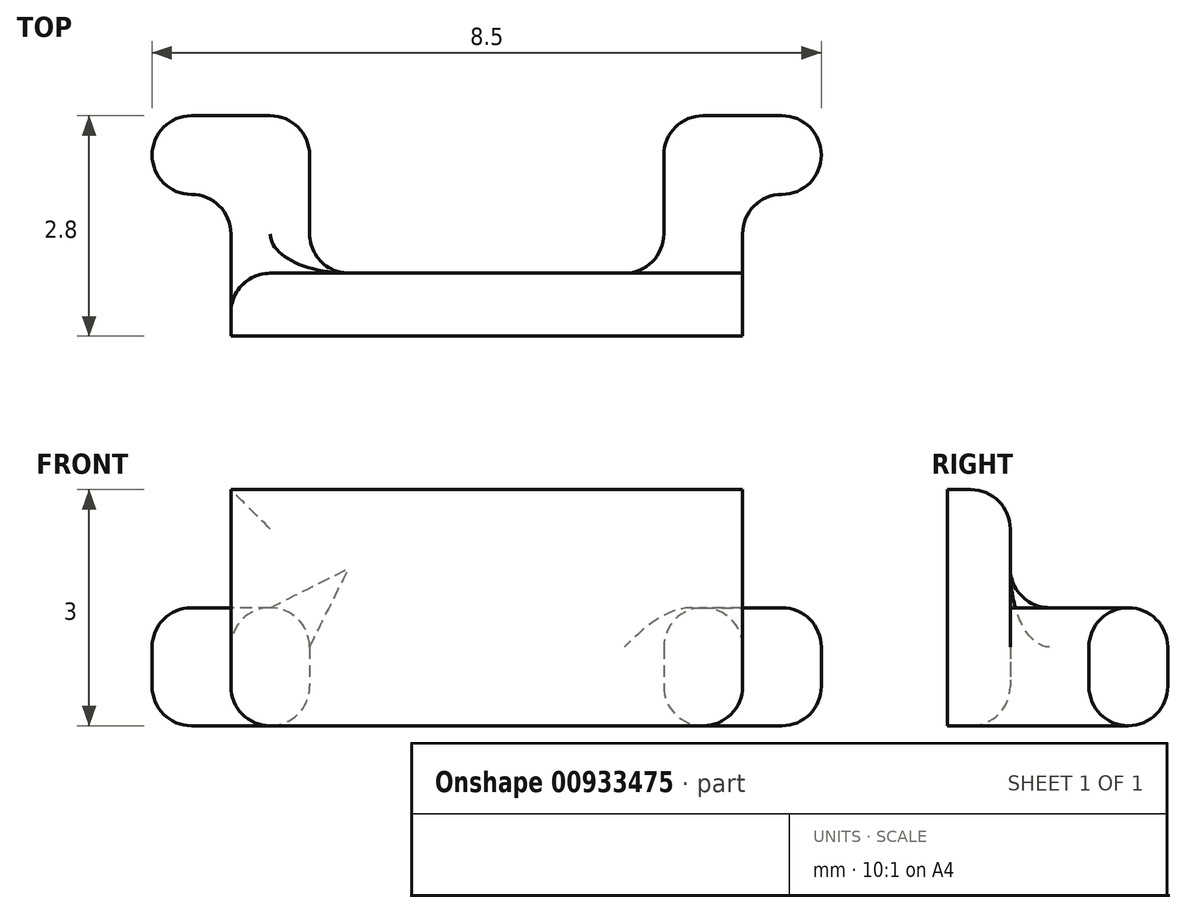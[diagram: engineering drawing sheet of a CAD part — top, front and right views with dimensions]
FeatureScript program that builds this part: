
annotation { "Feature Type Name" : "Feature", "Feature Type Description" : "" }
export const myFeature = defineFeature(function(context is Context, id is Id, definition is map)
    precondition{}
    {
        {
            var Q0;
            Q0=qCreatedBy(makeId("Top.planeOp"),FACE);
            var sketch = newSketch(context, id + "F0", { "sketchPlane" : qUnion([Q0])});
            skLineSegment(sketch, "E0", {"start": v(-3.25, 0) * mm, "end": v(3.25, 0) * mm});
            skPoint(sketch, "E1", {"position": v(0, 0) * mm});
            skLineSegment(sketch, "E2", {"start": v(0, -1.15) * mm, "end": v(0, 7.11) * mm, "construction": true});
            skLineSegment(sketch, "E3", {"start": v(2.25, 1.3) * mm, "end": v(2.25, 2.3) * mm});
            skLineSegment(sketch, "E4", {"start": v(-2.25, 1.3) * mm, "end": v(-2.25, 2.3) * mm});
            skLineSegment(sketch, "E5", {"start": v(-1.75, 0.8) * mm, "end": v(1.75, 0.8) * mm});
            skPoint(sketch, "E6", {"position": v(0, 0.8) * mm});
            skLineSegment(sketch, "E7", {"start": v(-2.75, 2.8) * mm, "end": v(-3.75, 2.8) * mm});
            skLineSegment(sketch, "E8", {"start": v(2.75, 2.8) * mm, "end": v(3.75, 2.8) * mm});
            skLineSegment(sketch, "E9", {"start": v(-4.25, 2.3) * mm, "end": v(-4.25, 2.3) * mm});
            skLineSegment(sketch, "E10", {"start": v(-3.75, 1.8) * mm, "end": v(-3.75, 1.8) * mm});
            skLineSegment(sketch, "E11", {"start": v(-3.25, 1.3) * mm, "end": v(-3.25, 1.3) * mm});
            skLineSegment(sketch, "E12", {"start": v(4.25, 2.3) * mm, "end": v(4.25, 2.3) * mm});
            skLineSegment(sketch, "E13", {"start": v(3.75, 1.8) * mm, "end": v(3.75, 1.8) * mm});
            skLineSegment(sketch, "E14", {"start": v(3.25, 1.3) * mm, "end": v(3.25, 1.3) * mm});
            skPoint(sketch, "E15.visualSharp", {"position": v(-2.25, 0.8) * mm});
            skArc(sketch, "E15.filletArc", {"start": v(-2.25, 1.3) * mm, "mid": v(-2.1, 0.95) * mm, "end": v(-1.75, 0.8) * mm});
            skPoint(sketch, "E16.visualSharp", {"position": v(2.25, 0.8) * mm});
            skArc(sketch, "E16.filletArc", {"start": v(1.75, 0.8) * mm, "mid": v(2.1, 0.95) * mm, "end": v(2.25, 1.3) * mm});
            skPoint(sketch, "E17.visualSharp", {"position": v(3.25, 1.8) * mm});
            skArc(sketch, "E17.filletArc", {"start": v(3.75, 1.8) * mm, "mid": v(3.4, 1.65) * mm, "end": v(3.25, 1.3) * mm});
            skPoint(sketch, "E18.visualSharp", {"position": v(-3.25, 1.8) * mm});
            skArc(sketch, "E18.filletArc", {"start": v(-3.25, 1.3) * mm, "mid": v(-3.4, 1.65) * mm, "end": v(-3.75, 1.8) * mm});
            skPoint(sketch, "E19.visualSharp", {"position": v(-2.25, 2.8) * mm});
            skArc(sketch, "E19.filletArc", {"start": v(-2.25, 2.3) * mm, "mid": v(-2.4, 2.65) * mm, "end": v(-2.75, 2.8) * mm});
            skPoint(sketch, "E20.visualSharp", {"position": v(2.25, 2.8) * mm});
            skArc(sketch, "E20.filletArc", {"start": v(2.75, 2.8) * mm, "mid": v(2.4, 2.65) * mm, "end": v(2.25, 2.3) * mm});
            skPoint(sketch, "E21.visualSharp", {"position": v(4.25, 2.8) * mm});
            skArc(sketch, "E21.filletArc", {"start": v(4.25, 2.3) * mm, "mid": v(4.1, 2.65) * mm, "end": v(3.75, 2.8) * mm});
            skPoint(sketch, "E22.visualSharp", {"position": v(4.25, 1.8) * mm});
            skArc(sketch, "E22.filletArc", {"start": v(3.75, 1.8) * mm, "mid": v(4.1, 1.95) * mm, "end": v(4.25, 2.3) * mm});
            skPoint(sketch, "E23.visualSharp", {"position": v(-4.25, 2.8) * mm});
            skArc(sketch, "E23.filletArc", {"start": v(-3.75, 2.8) * mm, "mid": v(-4.1, 2.65) * mm, "end": v(-4.25, 2.3) * mm});
            skPoint(sketch, "E24.visualSharp", {"position": v(-4.25, 1.8) * mm});
            skArc(sketch, "E24.filletArc", {"start": v(-4.25, 2.3) * mm, "mid": v(-4.1, 1.95) * mm, "end": v(-3.75, 1.8) * mm});
            skLineSegment(sketch, "E25", {"start": v(-3.25, 1.3) * mm, "end": v(-3.25, 0) * mm});
            skLineSegment(sketch, "E26", {"start": v(3.25, 1.3) * mm, "end": v(3.25, 0) * mm});
            skPoint(sketch, "E27.orphan", {"position": v(-5, 0) * mm});
            skPoint(sketch, "E28.orphan", {"position": v(5, 0) * mm});
            skSolve(sketch);
        }
        {
            var Q0;
            Q0 = qSketchRegion(id + "F0", true);
            extrude(context, id + "F1", {"entities" : qUnion([Q0]), "depth" : 1.5 * mm, "offsetDistance" : 25 * mm});
        }
        {
            var Q0;
            Q0=makeQuery(id+"F1.opExtrude","CAP_FACE",FACE,{"disambiguationData":[OSD([sQuery(id+"F0.wireOp",EDGE,"E0"),sQuery(id+"F0.wireOp",EDGE,"6YUp3G7D-HScl-yHn5-GseC-h8JY3a3RTnfq"),sQuery(id+"F0.wireOp",EDGE,"Xoj59s7T-2QtX-ZDX5-LiLJ-oQHR1xyVejqm"),sQuery(id+"F0.wireOp",EDGE,"Zc0sCTJD-TUej-OjTx-Aevo-d0EqPVeEhSTX"),sQuery(id+"F0.wireOp",EDGE,"E3"),sQuery(id+"F0.wireOp",EDGE,"E4"),sQuery(id+"F0.wireOp",EDGE,"fb0ed693-0343-43f7-9de8-dc647e30bef6.trimOffspring"),sQuery(id+"F0.wireOp",EDGE,"E5"),sQuery(id+"F0.wireOp",EDGE,"E7"),sQuery(id+"F0.wireOp",EDGE,"E8"),sQuery(id+"F0.wireOp",EDGE,"E15.filletArc"),sQuery(id+"F0.wireOp",EDGE,"E16.filletArc"),sQuery(id+"F0.wireOp",EDGE,"e3a1806a-2c86-475e-80ef-7f3d2f1d7afe.filletArc"),sQuery(id+"F0.wireOp",EDGE,"E17.filletArc"),sQuery(id+"F0.wireOp",EDGE,"63802826-9469-4e69-9e87-4bd683e02e6c.filletArc"),sQuery(id+"F0.wireOp",EDGE,"E18.filletArc"),sQuery(id+"F0.wireOp",EDGE,"E19.filletArc"),sQuery(id+"F0.wireOp",EDGE,"E20.filletArc"),sQuery(id+"F0.wireOp",EDGE,"E21.filletArc"),sQuery(id+"F0.wireOp",EDGE,"E22.filletArc"),sQuery(id+"F0.wireOp",EDGE,"E23.filletArc"),sQuery(id+"F0.wireOp",EDGE,"E24.filletArc")])],"isStart":false});
            var sketch = newSketch(context, id + "F2", { "sketchPlane" : qUnion([Q0])});
            skLineSegment(sketch, "E29.0", {"start": v(-3.25, 0) * mm, "end": v(-3.25, 0) * mm});
            skLineSegment(sketch, "E30.0", {"start": v(-3.25, 0) * mm, "end": v(-3.25, 0.8) * mm});
            skLineSegment(sketch, "E31", {"start": v(-3.25, 0.8) * mm, "end": v(3.25, 0.8) * mm});
            skLineSegment(sketch, "E32.0", {"start": v(-3.25, 0) * mm, "end": v(3.25, 0) * mm});
            skLineSegment(sketch, "E33.0", {"start": v(3.25, 0.8) * mm, "end": v(3.25, 0) * mm});
            skPoint(sketch, "E34.orphan", {"position": v(3.25, 1.3) * mm});
            skSolve(sketch);
        }
        {
            var Q0;
            Q0 = qSketchRegion(id + "F2", true);
            extrude(context, id + "F3", {"entities" : qUnion([Q0]), "operationType" : NewBodyOperationType.ADD, "depth" : 1.5 * mm, "offsetDistance" : 25 * mm});
        }
        {
            var Q0;
            {var subQ5=sQuery(id+"F0.wireOp",EDGE,"E15.filletArc");var subQ6=sQuery(id+"F2.wireOp",EDGE,"E31");Q0=makeQuery(id+"F3.boolean.opBoolean","SPLIT",EDGE,{"disambiguationData":[TD([makeQuery(id+"F1.opExtrude","SWEPT_FACE",FACE,{"disambiguationData":[OSD([subQ5])]})])],"derivedFrom":makeQuery(id+"F3.opExtrude","CAP_EDGE",EDGE,{"disambiguationData":[OSD([subQ6])],"isStart":true})});}
            var Q1;
            {var subQ5=sQuery(id+"F0.wireOp",EDGE,"E16.filletArc");var subQ6=sQuery(id+"F2.wireOp",EDGE,"E31");Q1=makeQuery(id+"F3.boolean.opBoolean","SPLIT",EDGE,{"disambiguationData":[TD([makeQuery(id+"F1.opExtrude","SWEPT_FACE",FACE,{"disambiguationData":[OSD([subQ5])]})])],"derivedFrom":makeQuery(id+"F3.opExtrude","CAP_EDGE",EDGE,{"disambiguationData":[OSD([subQ6])],"isStart":true})});}
            fillet(context, id + "F4", {"entities" : qUnion([Q0, Q1]), "radius" : 0.5 * mm, "tangentPropagation" : true, "allowEdgeOverflow" : false});
        }
        {
            var Q0;
            Q0=makeQuery(id+"F3.opExtrude","CAP_EDGE",EDGE,{"disambiguationData":[OSD([sQuery(id+"F2.wireOp",EDGE,"E31")])],"isStart":false});
            var Q1;
            Q1=makeQuery(id+"F1.opExtrude","CAP_EDGE",EDGE,{"disambiguationData":[OSD([sQuery(id+"F0.wireOp",EDGE,"E8")])],"isStart":false});
            var Q2;
            Q2=makeQuery(id+"F1.opExtrude","CAP_EDGE",EDGE,{"disambiguationData":[OSD([sQuery(id+"F0.wireOp",EDGE,"E7")])],"isStart":false});
            var Q3;
            Q3=makeQuery(id+"F3.boolean.opBoolean","MERGE",EDGE,{"derivedFrom":[makeQuery(id+"F1.opExtrude","SWEPT_EDGE",EDGE,{"disambiguationData":[OSD([sQuery(id+"F0.wireOp",EDGE,"6YUp3G7D-HScl-yHn5-GseC-h8JY3a3RTnfq"),sQuery(id+"F0.wireOp",EDGE,"Xoj59s7T-2QtX-ZDX5-LiLJ-oQHR1xyVejqm")])]}),makeQuery(id+"F3.opExtrude","SWEPT_EDGE",EDGE,{"disambiguationData":[OSD([sQuery(id+"F2.wireOp",EDGE,"E30.0"),sQuery(id+"F2.wireOp",EDGE,"E31")])]})]});
            var Q4;
            Q4=makeQuery(id+"F3.boolean.opBoolean","MERGE",EDGE,{"derivedFrom":[makeQuery(id+"F1.opExtrude","SWEPT_EDGE",EDGE,{"disambiguationData":[OSD([sQuery(id+"F0.wireOp",EDGE,"Zc0sCTJD-TUej-OjTx-Aevo-d0EqPVeEhSTX"),sQuery(id+"F0.wireOp",EDGE,"fb0ed693-0343-43f7-9de8-dc647e30bef6.trimOffspring")])]}),makeQuery(id+"F3.opExtrude","SWEPT_EDGE",EDGE,{"disambiguationData":[OSD([sQuery(id+"F2.wireOp",EDGE,"d5f53f8e-ae0b-4405-8b29-70071fd9f723.0"),sQuery(id+"F2.wireOp",EDGE,"E31")])]})]});
            var Q5;
            Q5=makeQuery(id+"F1.opExtrude","CAP_EDGE",EDGE,{"disambiguationData":[OSD([sQuery(id+"F0.wireOp",EDGE,"E5")])],"isStart":true});
            fillet(context, id + "F5", {"entities" : qUnion([Q0, Q1, Q2, Q3, Q4, Q5]), "radius" : 0.5 * mm, "tangentPropagation" : true, "defaultsChanged" : false, "vertexSettings" : [], "allowEdgeOverflow" : false});
        }
    });
